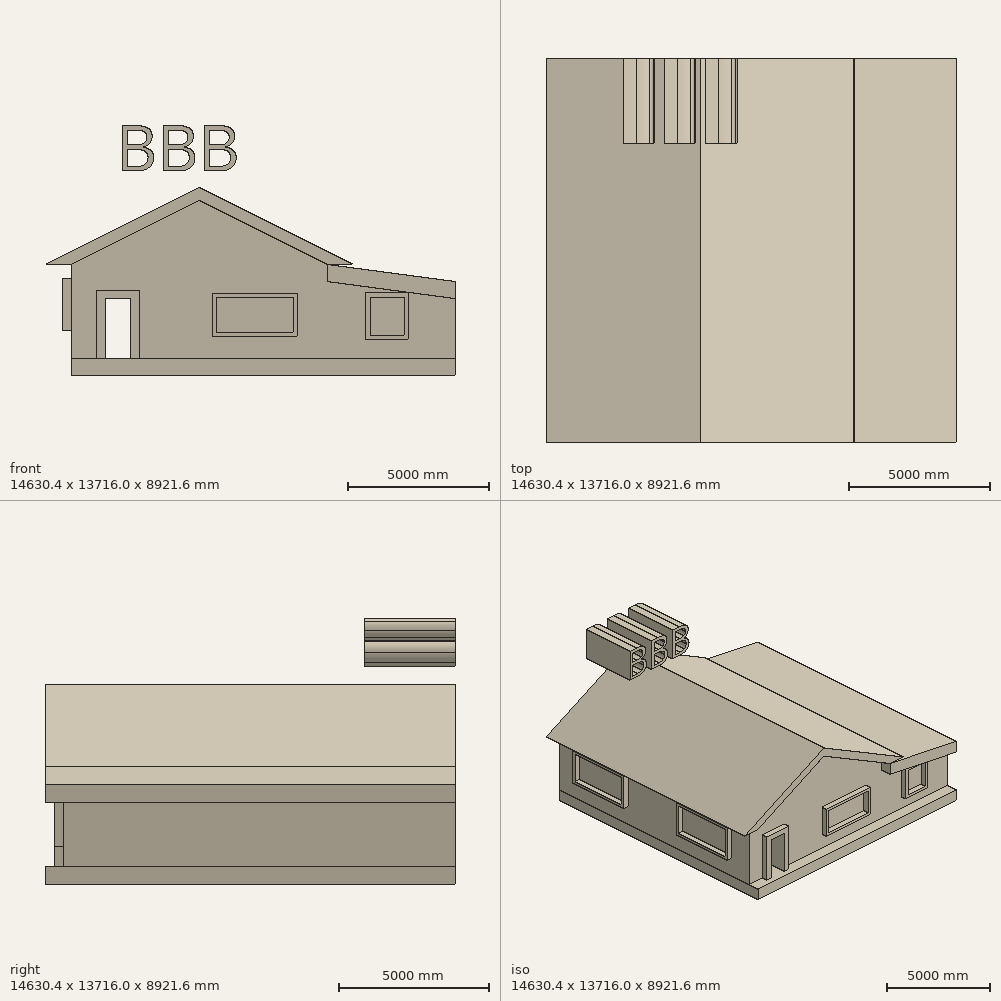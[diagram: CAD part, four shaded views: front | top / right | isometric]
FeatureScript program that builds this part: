
annotation { "Feature Type Name" : "Feature", "Feature Type Description" : "" }
export const myFeature = defineFeature(function(context is Context, id is Id, definition is map)
    precondition{}
    {
        {
            var Q0;
            Q0=qCreatedBy(makeId("Front.planeOp"),FACE);
            var sketch = newSketch(context, id + "F0", { "sketchPlane" : qUnion([Q0])});
            skLineSegment(sketch, "E0", {"start": v(0, 0) * mm, "end": v(-4572, 0) * mm});
            skLineSegment(sketch, "E1", {"start": v(0, 0) * mm, "end": v(4572, 0) * mm});
            skLineSegment(sketch, "E2", {"start": v(0, 0) * mm, "end": v(0, 2286) * mm, "construction": true});
            skLineSegment(sketch, "E3", {"start": v(0, 2286) * mm, "end": v(4572, 0) * mm});
            skLineSegment(sketch, "E4", {"start": v(0, 2286) * mm, "end": v(-4572, 0) * mm});
            skLineSegment(sketch, "E5", {"start": v(0, 2286) * mm, "end": v(0, 2743.2) * mm});
            skLineSegment(sketch, "E6", {"start": v(-4572, 0) * mm, "end": v(-5486.4, 0) * mm});
            skLineSegment(sketch, "E7", {"start": v(4572, 0) * mm, "end": v(5486.4, 0) * mm});
            skLineSegment(sketch, "E8", {"start": v(0, 2743.2) * mm, "end": v(5486.4, 0) * mm});
            skLineSegment(sketch, "E9", {"start": v(0, 2743.2) * mm, "end": v(-5486.4, 0) * mm});
            skLineSegment(sketch, "E10", {"start": v(-4572, 0) * mm, "end": v(-4572, -3352.8) * mm});
            skLineSegment(sketch, "E11", {"start": v(4572, 0) * mm, "end": v(4572, -3352.8) * mm});
            skLineSegment(sketch, "E12", {"start": v(4572, -3352.8) * mm, "end": v(-4572, -3352.8) * mm});
            skLineSegment(sketch, "E13", {"start": v(-4572, -3352.8) * mm, "end": v(-4572, -3962.4) * mm});
            skLineSegment(sketch, "E14", {"start": v(4572, -3352.8) * mm, "end": v(4572, -3962.4) * mm});
            skLineSegment(sketch, "E15", {"start": v(4572, -3962.4) * mm, "end": v(-4572, -3962.4) * mm});
            skLineSegment(sketch, "E16", {"start": v(4572, -3352.8) * mm, "end": v(9144, -3352.8) * mm});
            skLineSegment(sketch, "E17", {"start": v(9144, -3352.8) * mm, "end": v(9144, -3962.4) * mm});
            skLineSegment(sketch, "E18", {"start": v(9144, -3962.4) * mm, "end": v(4572, -3962.4) * mm});
            skLineSegment(sketch, "E19", {"start": v(9144, -3352.8) * mm, "end": v(9144, -609.6) * mm});
            skLineSegment(sketch, "E20", {"start": v(4572, 0) * mm, "end": v(9144, -609.6) * mm});
            skLineSegment(sketch, "E21.bottom", {"start": v(-3352.8, -3352.8) * mm, "end": v(-2438.4, -3352.8) * mm});
            skLineSegment(sketch, "E21.top", {"start": v(-3352.8, -1219.2) * mm, "end": v(-2438.4, -1219.2) * mm});
            skLineSegment(sketch, "E21.left", {"start": v(-3352.8, -3352.8) * mm, "end": v(-3352.8, -1219.2) * mm});
            skLineSegment(sketch, "E21.right", {"start": v(-2438.4, -3352.8) * mm, "end": v(-2438.4, -1219.2) * mm});
            skLineSegment(sketch, "E22.0", {"start": v(-3657.6, -3352.8) * mm, "end": v(-3657.6, -914.4) * mm});
            skLineSegment(sketch, "E22.1", {"start": v(-3657.6, -914.4) * mm, "end": v(-2133.6, -914.4) * mm});
            skLineSegment(sketch, "E22.2", {"start": v(-2133.6, -3352.8) * mm, "end": v(-2133.6, -914.4) * mm});
            skLineSegment(sketch, "E23.bottom", {"start": v(609.6, -2410.46) * mm, "end": v(3352.8, -2410.46) * mm});
            skLineSegment(sketch, "E23.top", {"start": v(609.6, -1191.26) * mm, "end": v(3352.8, -1191.26) * mm});
            skLineSegment(sketch, "E23.left", {"start": v(609.6, -2410.46) * mm, "end": v(609.6, -1191.26) * mm});
            skLineSegment(sketch, "E23.right", {"start": v(3352.8, -2410.46) * mm, "end": v(3352.8, -1191.26) * mm});
            skLineSegment(sketch, "E24.0", {"start": v(457.2, -1038.86) * mm, "end": v(3505.2, -1038.86) * mm});
            skLineSegment(sketch, "E24.1", {"start": v(457.2, -2562.86) * mm, "end": v(457.2, -1038.86) * mm});
            skLineSegment(sketch, "E24.2", {"start": v(457.2, -2562.86) * mm, "end": v(3505.2, -2562.86) * mm});
            skLineSegment(sketch, "E24.3", {"start": v(3505.2, -2562.86) * mm, "end": v(3505.2, -1038.86) * mm});
            skLineSegment(sketch, "E25", {"start": v(4572, -609.6) * mm, "end": v(9144, -1219.2) * mm});
            skLineSegment(sketch, "E26.bottom", {"start": v(6096, -2533.13) * mm, "end": v(7315.2, -2533.13) * mm});
            skLineSegment(sketch, "E26.top", {"start": v(6096, -1161.53) * mm, "end": v(7315.2, -1161.53) * mm});
            skLineSegment(sketch, "E26.left", {"start": v(6096, -2533.13) * mm, "end": v(6096, -1161.53) * mm});
            skLineSegment(sketch, "E26.right", {"start": v(7315.2, -2533.13) * mm, "end": v(7315.2, -1161.53) * mm});
            skLineSegment(sketch, "E27.0", {"start": v(6101, -1166.53) * mm, "end": v(7310.2, -1166.53) * mm});
            skLineSegment(sketch, "E27.1", {"start": v(6101, -2528.13) * mm, "end": v(6101, -1166.53) * mm});
            skLineSegment(sketch, "E27.2", {"start": v(6101, -2528.13) * mm, "end": v(7310.2, -2528.13) * mm});
            skLineSegment(sketch, "E27.3", {"start": v(7310.2, -2528.13) * mm, "end": v(7310.2, -1166.53) * mm});
            skLineSegment(sketch, "E28.0", {"start": v(5943.6, -1009.13) * mm, "end": v(7467.6, -1009.13) * mm});
            skLineSegment(sketch, "E28.1", {"start": v(5943.6, -2685.53) * mm, "end": v(5943.6, -1009.13) * mm});
            skLineSegment(sketch, "E28.2", {"start": v(5943.6, -2685.53) * mm, "end": v(7467.6, -2685.53) * mm});
            skLineSegment(sketch, "E28.3", {"start": v(7467.6, -2685.53) * mm, "end": v(7467.6, -1009.13) * mm});
            skText(sketch, "E29", { "text": "BBB", "fontName": "OpenSans-Regular.ttf"});
            const initialGuessF0  = {"E29": [-2.97213, 3.33743, 1, 0, 1.63564]};
            skSetInitialGuess(sketch, initialGuessF0);
            skSolve(sketch);
        }
        {
            var Q0;
            Q0=makeQuery(id+"F0.imprint","IMPRINT",FACE,{"disambiguationData":[TD([[makeQuery(id+"F0.imprint","IMPRINT",EDGE,{"derivedFrom":sQuery(id+"F0.wireOp",EDGE,"E3")}),1.0]])]});
            var Q1;
            Q1=makeQuery(id+"F0.imprint","IMPRINT",FACE,{"disambiguationData":[TD([[makeQuery(id+"F0.imprint","IMPRINT",EDGE,{"derivedFrom":sQuery(id+"F0.wireOp",EDGE,"E4")}),-1.0]])]});
            var Q2;
            {var subQ0=sQuery(id+"F0.wireOp",EDGE,"E20");Q2=makeQuery(id+"F0.imprint","IMPRINT",FACE,{"disambiguationData":[TD([[makeQuery(id+"F0.imprint","IMPRINT",EDGE,{"derivedFrom":subQ0}),-1.0]])]});}
            var Q3;
            Q3=makeQuery(id+"F0.imprint","IMPRINT",FACE,{"disambiguationData":[TD([[makeQuery(id+"F0.imprint","IMPRINT",EDGE,{"derivedFrom":sQuery(id+"F0.wireOp",EDGE,"E14")}),1.0]])]});
            var Q4;
            {var subQ0=sQuery(id+"F0.wireOp",EDGE,"E13");Q4=makeQuery(id+"F0.imprint","IMPRINT",FACE,{"disambiguationData":[TD([[makeQuery(id+"F0.imprint","IMPRINT",EDGE,{"derivedFrom":subQ0}),1.0]])]});}
            extrude(context, id + "F1", {"entities" : qUnion([Q0, Q1, Q2, Q3, Q4]), "depth" : 13716 * mm, "offsetDistance" : 30.48 * mm});
        }
        {
            var Q0;
            Q0=makeQuery(id+"F0.imprint","IMPRINT",FACE,{"disambiguationData":[TD([[makeQuery(id+"F0.imprint","IMPRINT",EDGE,{"derivedFrom":sQuery(id+"F0.wireOp",EDGE,"E0")}),1.0]])]});
            var Q1;
            {var subQ2=sQuery(id+"F0.wireOp",EDGE,"E16");Q1=makeQuery(id+"F0.imprint","IMPRINT",FACE,{"disambiguationData":[TD([[makeQuery(id+"F0.imprint","IMPRINT",EDGE,{"derivedFrom":subQ2}),1.0]])]});}
            var Q2;
            Q2=makeQuery(id+"F0.imprint","IMPRINT",FACE,{"disambiguationData":[TD([[makeQuery(id+"F0.imprint","IMPRINT",EDGE,{"derivedFrom":sQuery(id+"F0.wireOp",EDGE,"E0")}),-1.0]])]});
            var Q3;
            Q3=makeQuery(id+"F0.imprint","IMPRINT",FACE,{"disambiguationData":[TD([[makeQuery(id+"F0.imprint","IMPRINT",EDGE,{"derivedFrom":sQuery(id+"F0.wireOp",EDGE,"E21.bottom")}),1.0]])]});
            var Q4;
            Q4=makeQuery(id+"F0.imprint","IMPRINT",FACE,{"disambiguationData":[TD([[makeQuery(id+"F0.imprint","IMPRINT",EDGE,{"derivedFrom":sQuery(id+"F0.wireOp",EDGE,"E23.bottom")}),1.0]])]});
            var Q5;
            Q5=makeQuery(id+"F0.imprint","IMPRINT",FACE,{"disambiguationData":[TD([[makeQuery(id+"F0.imprint","IMPRINT",EDGE,{"derivedFrom":sQuery(id+"F0.wireOp",EDGE,"E27.0")}),-1.0]])]});
            extrude(context, id + "F2", {"entities" : qUnion([Q0, Q1, Q2, Q3, Q4, Q5]), "depth" : 13106.4 * mm, "offsetDistance" : 30.48 * mm});
        }
        {
            var Q0;
            Q0=makeQuery(id+"F0.imprint","IMPRINT",FACE,{"disambiguationData":[TD([[makeQuery(id+"F0.imprint","IMPRINT",EDGE,{"derivedFrom":sQuery(id+"F0.wireOp",EDGE,"E21.top")}),1.0]])]});
            var Q1;
            Q1=makeQuery(id+"F0.imprint","IMPRINT",FACE,{"disambiguationData":[TD([[makeQuery(id+"F0.imprint","IMPRINT",EDGE,{"derivedFrom":sQuery(id+"F0.wireOp",EDGE,"E23.bottom")}),-1.0]])]});
            var Q2;
            Q2=makeQuery(id+"F0.imprint","IMPRINT",FACE,{"disambiguationData":[TD([[makeQuery(id+"F0.imprint","IMPRINT",EDGE,{"derivedFrom":sQuery(id+"F0.wireOp",EDGE,"E26.bottom")}),-1.0]])]});
            extrude(context, id + "F3", {"entities" : qUnion([Q0, Q1, Q2]), "depth" : 13411.2 * mm, "offsetDistance" : 30.48 * mm});
        }
        {
            var Q0;
            Q0=makeQuery(id+"F2.opExtrude","SWEPT_FACE",FACE,{"disambiguationData":[OSD([sQuery(id+"F0.wireOp",EDGE,"E10")])]});
            var sketch = newSketch(context, id + "F4", { "sketchPlane" : qUnion([Q0])});
            skLineSegment(sketch, "E30.bottom", {"start": v(1370.1, -667.55) * mm, "end": v(4585.44, -667.55) * mm});
            skLineSegment(sketch, "E30.top", {"start": v(1370.1, -2200.39) * mm, "end": v(4585.44, -2200.39) * mm});
            skLineSegment(sketch, "E30.left", {"start": v(1370.1, -667.55) * mm, "end": v(1370.1, -2200.39) * mm});
            skLineSegment(sketch, "E30.right", {"start": v(4585.44, -667.55) * mm, "end": v(4585.44, -2200.39) * mm});
            skLineSegment(sketch, "E31.0", {"start": v(4737.84, -515.15) * mm, "end": v(4737.84, -2352.79) * mm});
            skLineSegment(sketch, "E31.1", {"start": v(1217.7, -515.15) * mm, "end": v(4737.84, -515.15) * mm});
            skLineSegment(sketch, "E31.2", {"start": v(1217.7, -515.15) * mm, "end": v(1217.7, -2352.79) * mm});
            skLineSegment(sketch, "E31.3", {"start": v(1217.7, -2352.79) * mm, "end": v(4737.84, -2352.79) * mm});
            skLineSegment(sketch, "E32.bottom", {"start": v(8520.99, -667.51) * mm, "end": v(11736.32, -667.51) * mm});
            skLineSegment(sketch, "E32.top", {"start": v(8520.99, -2200.35) * mm, "end": v(11736.32, -2200.35) * mm});
            skLineSegment(sketch, "E32.left", {"start": v(8520.99, -667.51) * mm, "end": v(8520.99, -2200.35) * mm});
            skLineSegment(sketch, "E32.right", {"start": v(11736.32, -667.51) * mm, "end": v(11736.32, -2200.35) * mm});
            skLineSegment(sketch, "E33.0", {"start": v(8368.59, -515.11) * mm, "end": v(11888.72, -515.11) * mm});
            skLineSegment(sketch, "E33.1", {"start": v(8368.59, -515.11) * mm, "end": v(8368.59, -2352.75) * mm});
            skLineSegment(sketch, "E33.2", {"start": v(8368.59, -2352.75) * mm, "end": v(11888.72, -2352.75) * mm});
            skLineSegment(sketch, "E33.3", {"start": v(11888.72, -515.11) * mm, "end": v(11888.72, -2352.75) * mm});
            skSolve(sketch);
        }
        {
            var Q0;
            Q0=makeQuery(id+"F4.imprint","IMPRINT",FACE,{"disambiguationData":[TD([[makeQuery(id+"F4.imprint","IMPRINT",EDGE,{"derivedFrom":sQuery(id+"F4.wireOp",EDGE,"E30.bottom")}),1.0]])]});
            var Q1;
            Q1=makeQuery(id+"F4.imprint","IMPRINT",FACE,{"disambiguationData":[TD([[makeQuery(id+"F4.imprint","IMPRINT",EDGE,{"derivedFrom":sQuery(id+"F4.wireOp",EDGE,"E32.bottom")}),1.0]])]});
            extrude(context, id + "F5", {"entities" : qUnion([Q0, Q1]), "operationType" : NewBodyOperationType.ADD, "depth" : 304.8 * mm, "offsetDistance" : 30.48 * mm});
        }
        {
            var Q0;
            Q0=makeQuery(id+"F0.imprint","IMPRINT",FACE,{"disambiguationData":[TD([[makeQuery(id+"F0.imprint","IMPRINT",EDGE,{"derivedFrom":sQuery(id+"F0.wireOp",EDGE,"E29.sketch_text.stroke-0")}),-1.0]])]});
            var Q1;
            Q1=makeQuery(id+"F0.imprint","IMPRINT",FACE,{"disambiguationData":[TD([[makeQuery(id+"F0.imprint","IMPRINT",EDGE,{"derivedFrom":sQuery(id+"F0.wireOp",EDGE,"E29.sketch_text.stroke-25")}),-1.0]])]});
            var Q2;
            Q2=makeQuery(id+"F0.imprint","IMPRINT",FACE,{"disambiguationData":[TD([[makeQuery(id+"F0.imprint","IMPRINT",EDGE,{"derivedFrom":sQuery(id+"F0.wireOp",EDGE,"E29.sketch_text.stroke-50")}),-1.0]])]});
            extrude(context, id + "F6", {"entities" : qUnion([Q0, Q1, Q2]), "depth" : 3048 * mm, "offsetDistance" : 30.48 * mm});
        }
    });
